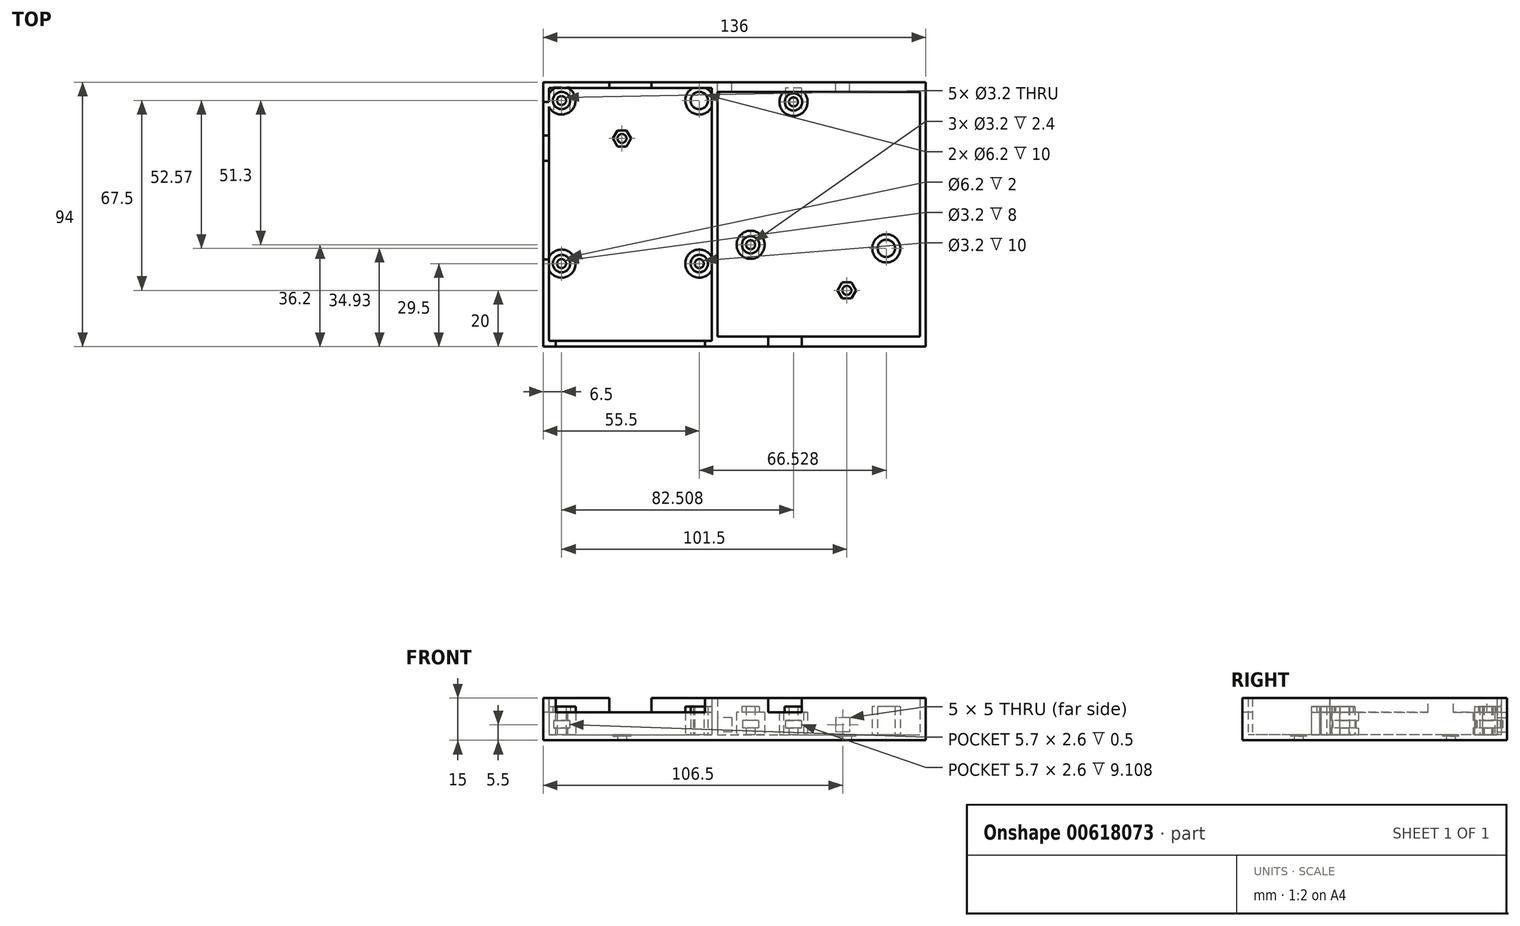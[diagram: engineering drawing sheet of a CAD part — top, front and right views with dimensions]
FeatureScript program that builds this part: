
annotation { "Feature Type Name" : "Feature", "Feature Type Description" : "" }
export const myFeature = defineFeature(function(context is Context, id is Id, definition is map)
    precondition{}
    {
        {
            var Q0;
            Q0=qCreatedBy(makeId("Top.planeOp"),FACE);
            var sketch = newSketch(context, id + "F0", { "sketchPlane" : qUnion([Q0])});
            skLineSegment(sketch, "E0.bottom", {"start": v(-9, 44) * mm, "end": v(-65, 44) * mm, "construction": true});
            skLineSegment(sketch, "E0.top", {"start": v(-9, -44) * mm, "end": v(-65, -44) * mm, "construction": true});
            skLineSegment(sketch, "E0.left", {"start": v(-9, 44) * mm, "end": v(-9, -44) * mm, "construction": true});
            skLineSegment(sketch, "E0.right", {"start": v(-65, 44) * mm, "end": v(-65, -44) * mm, "construction": true});
            skLineSegment(sketch, "E1.bottom", {"start": v(-68, 47) * mm, "end": v(68, 47) * mm});
            skLineSegment(sketch, "E1.top", {"start": v(-68, -47) * mm, "end": v(68, -47) * mm});
            skLineSegment(sketch, "E1.left", {"start": v(-68, 47) * mm, "end": v(-68, -47) * mm});
            skLineSegment(sketch, "E1.right", {"start": v(68, 47) * mm, "end": v(68, -47) * mm});
            skPoint(sketch, "E2", {"position": v(5.77, -10.8) * mm});
            skPoint(sketch, "E3", {"position": v(54.03, -12.07) * mm});
            skPoint(sketch, "E4", {"position": v(21, 40) * mm});
            skPoint(sketch, "E5", {"position": v(-61.5, 40.5) * mm});
            skPoint(sketch, "E6", {"position": v(-12.5, 40.5) * mm});
            skPoint(sketch, "E7", {"position": v(-12.5, -17.5) * mm});
            skPoint(sketch, "E8", {"position": v(-61.5, -17.5) * mm});
            skLineSegment(sketch, "E9.bottom", {"start": v(-61.5, 40.5) * mm, "end": v(-12.5, 40.5) * mm, "construction": true});
            skLineSegment(sketch, "E9.top", {"start": v(-61.5, -17.5) * mm, "end": v(-12.5, -17.5) * mm, "construction": true});
            skLineSegment(sketch, "E9.left", {"start": v(-61.5, 40.5) * mm, "end": v(-61.5, -17.5) * mm, "construction": true});
            skLineSegment(sketch, "E9.right", {"start": v(-12.5, 40.5) * mm, "end": v(-12.5, -17.5) * mm, "construction": true});
            skLineSegment(sketch, "E10.bottom", {"start": v(-8, -45) * mm, "end": v(-66, -45) * mm});
            skLineSegment(sketch, "E10.top", {"start": v(-8, 45) * mm, "end": v(-66, 45) * mm});
            skLineSegment(sketch, "E10.left", {"start": v(-8, -45) * mm, "end": v(-8, 45) * mm});
            skLineSegment(sketch, "E10.right", {"start": v(-66, -45) * mm, "end": v(-66, 45) * mm});
            skLineSegment(sketch, "E11.bottom", {"start": v(66, -43.5) * mm, "end": v(-6, -43.5) * mm});
            skLineSegment(sketch, "E11.top", {"start": v(66, 43.5) * mm, "end": v(-6, 43.5) * mm});
            skLineSegment(sketch, "E11.left", {"start": v(66, -43.5) * mm, "end": v(66, 43.5) * mm});
            skLineSegment(sketch, "E11.right", {"start": v(-6, -43.5) * mm, "end": v(-6, 43.5) * mm});
            skPoint(sketch, "E11.middle", {"position": v(30, 0) * mm});
            skLineSegment(sketch, "E12.bottom", {"start": v(65, -42.5) * mm, "end": v(-5, -42.5) * mm, "construction": true});
            skLineSegment(sketch, "E12.top", {"start": v(65, 42.5) * mm, "end": v(-5, 42.5) * mm, "construction": true});
            skLineSegment(sketch, "E12.left", {"start": v(65, -42.5) * mm, "end": v(65, 42.5) * mm, "construction": true});
            skLineSegment(sketch, "E12.right", {"start": v(-5, -42.5) * mm, "end": v(-5, 42.5) * mm, "construction": true});
            skPoint(sketch, "E13", {"position": v(-37, 0) * mm});
            skPoint(sketch, "E13.positionSnap0", {"position": v(-37, 45) * mm});
            skPoint(sketch, "E13.positionSnap1", {"position": v(-8, 0) * mm});
            skSolve(sketch);
        }
        {
            var Q0;
            Q0=makeQuery(id+"F0.imprint","IMPRINT",FACE,{"disambiguationData":[TD([[makeQuery(id+"F0.imprint","IMPRINT",EDGE,{"derivedFrom":sQuery(id+"F0.wireOp",EDGE,"E1.bottom")}),-1.0]])]});
            var Q1;
            Q1=makeQuery(id+"F0.imprint","IMPRINT",FACE,{"disambiguationData":[TD([[makeQuery(id+"F0.imprint","IMPRINT",EDGE,{"derivedFrom":sQuery(id+"F0.wireOp",EDGE,"E11.bottom")}),-1.0]])]});
            var Q2;
            Q2=makeQuery(id+"F0.imprint","IMPRINT",FACE,{"disambiguationData":[TD([[makeQuery(id+"F0.imprint","IMPRINT",EDGE,{"derivedFrom":sQuery(id+"F0.wireOp",EDGE,"E10.bottom")}),-1.0]])]});
            extrude(context, id + "F1", {"entities" : qUnion([Q0, Q1, Q2]), "depth" : 2 * mm, "offsetDistance" : 25 * mm});
        }
        {
            var Q0;
            Q0=makeQuery(id+"F0.imprint","IMPRINT",FACE,{"disambiguationData":[TD([[makeQuery(id+"F0.imprint","IMPRINT",EDGE,{"derivedFrom":sQuery(id+"F0.wireOp",EDGE,"E1.bottom")}),-1.0]])]});
            extrude(context, id + "F2", {"entities" : qUnion([Q0]), "operationType" : NewBodyOperationType.ADD, "depth" : 15 * mm, "offsetDistance" : 25 * mm});
        }
        {
            var Q0;
            Q0=makeQuery(id+"F2.boolean.opBoolean","SPLIT",FACE,{"disambiguationData":[TD([makeQuery(id+"F2.opExtrude","SWEPT_FACE",FACE,{"disambiguationData":[OSD([sQuery(id+"F0.wireOp",EDGE,"E10.bottom")])]})])],"derivedFrom":makeQuery(id+"F1.opExtrude","CAP_FACE",FACE,{"disambiguationData":[OSD([sQuery(id+"F0.wireOp",EDGE,"E1.bottom"),sQuery(id+"F0.wireOp",EDGE,"E1.top"),sQuery(id+"F0.wireOp",EDGE,"E1.left"),sQuery(id+"F0.wireOp",EDGE,"E1.right")])],"isStart":false})});
            var sketch = newSketch(context, id + "F3", { "sketchPlane" : qUnion([Q0])});
            skCircle(sketch, "E14", {"center": v(-61.5, 40.5) * mm, "radius": 5 * mm});
            skCircle(sketch, "E15", {"center": v(-61.5, 40.5) * mm, "radius": 3.1 * mm});
            skCircle(sketch, "E16", {"center": v(-61.5, 40.5) * mm, "radius": 1.6 * mm});
            skLineSegment(sketch, "E17", {"start": v(-37, 64.72) * mm, "end": v(-37, -33.51) * mm, "construction": true});
            skCircle(sketch, "E18.MirrorC", {"center": v(-12.5, 40.5) * mm, "radius": 5 * mm});
            skCircle(sketch, "E19.MirrorC", {"center": v(-12.5, 40.5) * mm, "radius": 3.1 * mm});
            skCircle(sketch, "E20.MirrorC", {"center": v(-12.5, 40.5) * mm, "radius": 1.6 * mm});
            skLineSegment(sketch, "E21", {"start": v(-88.41, 11.5) * mm, "end": v(-11.99, 11.5) * mm, "construction": true});
            skCircle(sketch, "E22.MirrorC", {"center": v(-61.5, -17.5) * mm, "radius": 5 * mm});
            skCircle(sketch, "E23.MirrorC", {"center": v(-61.5, -17.5) * mm, "radius": 3.1 * mm});
            skCircle(sketch, "E24.MirrorC", {"center": v(-61.5, -17.5) * mm, "radius": 1.6 * mm});
            skCircle(sketch, "E25.MirrorC", {"center": v(-12.5, -17.5) * mm, "radius": 5 * mm});
            skCircle(sketch, "E26.MirrorC", {"center": v(-12.5, -17.5) * mm, "radius": 3.1 * mm});
            skCircle(sketch, "E27.MirrorC", {"center": v(-12.5, -17.5) * mm, "radius": 1.6 * mm});
            skCircle(sketch, "E28", {"center": v(5.77, -10.8) * mm, "radius": 1.6 * mm});
            skCircle(sketch, "E29", {"center": v(5.77, -10.8) * mm, "radius": 3.1 * mm});
            skCircle(sketch, "E30", {"center": v(5.77, -10.8) * mm, "radius": 5 * mm});
            skLineSegment(sketch, "E31", {"start": v(35.4, 26.87) * mm, "end": v(35.4, -34.45) * mm, "construction": true});
            skCircle(sketch, "E32.MirrorC", {"center": v(54.03, -12.07) * mm, "radius": 5 * mm});
            skCircle(sketch, "E33.MirrorC", {"center": v(54.03, -12.07) * mm, "radius": 3.1 * mm});
            skCircle(sketch, "E34.MirrorC", {"center": v(54.03, -12.07) * mm, "radius": 1.6 * mm});
            skCircle(sketch, "E35", {"center": v(21, 40) * mm, "radius": 1.6 * mm});
            skCircle(sketch, "E36", {"center": v(21, 40) * mm, "radius": 3.1 * mm});
            skCircle(sketch, "E37", {"center": v(21, 40) * mm, "radius": 5 * mm});
            skSolve(sketch);
        }
        {
            var Q0;
            Q0=makeQuery(id+"F3.imprint","IMPRINT",FACE,{"disambiguationData":[TD([[makeQuery(id+"F3.imprint","IMPRINT",EDGE,{"derivedFrom":sQuery(id+"F3.wireOp",EDGE,"E15")}),1.0]])]});
            var Q1;
            Q1=makeQuery(id+"F3.imprint","IMPRINT",FACE,{"disambiguationData":[TD([[makeQuery(id+"F3.imprint","IMPRINT",EDGE,{"derivedFrom":sQuery(id+"F3.wireOp",EDGE,"E19.MirrorC")}),-1.0]])]});
            var Q2;
            Q2=makeQuery(id+"F3.imprint","IMPRINT",FACE,{"disambiguationData":[TD([[makeQuery(id+"F3.imprint","IMPRINT",EDGE,{"derivedFrom":sQuery(id+"F3.wireOp",EDGE,"E23.MirrorC")}),-1.0]])]});
            var Q3;
            Q3=makeQuery(id+"F3.imprint","IMPRINT",FACE,{"disambiguationData":[TD([[makeQuery(id+"F3.imprint","IMPRINT",EDGE,{"derivedFrom":sQuery(id+"F3.wireOp",EDGE,"E26.MirrorC")}),1.0]])]});
            var Q4;
            Q4=makeQuery(id+"F3.imprint","IMPRINT",FACE,{"disambiguationData":[TD([[makeQuery(id+"F3.imprint","IMPRINT",EDGE,{"derivedFrom":sQuery(id+"F3.wireOp",EDGE,"E28")}),-1.0]])]});
            var Q5;
            Q5=makeQuery(id+"F3.imprint","IMPRINT",FACE,{"disambiguationData":[TD([[makeQuery(id+"F3.imprint","IMPRINT",EDGE,{"derivedFrom":sQuery(id+"F3.wireOp",EDGE,"E33.MirrorC")}),-1.0]])]});
            var Q6;
            Q6=makeQuery(id+"F3.imprint","IMPRINT",FACE,{"disambiguationData":[TD([[makeQuery(id+"F3.imprint","IMPRINT",EDGE,{"derivedFrom":sQuery(id+"F3.wireOp",EDGE,"E35")}),-1.0]])]});
            extrude(context, id + "F4", {"entities" : qUnion([Q0, Q1, Q2, Q3, Q4, Q5, Q6]), "operationType" : NewBodyOperationType.ADD, "depth" : 10 * mm, "offsetDistance" : 25 * mm});
        }
        {
            var Q0;
            Q0=makeQuery(id+"F3.imprint","IMPRINT",FACE,{"disambiguationData":[TD([[makeQuery(id+"F3.imprint","IMPRINT",EDGE,{"derivedFrom":sQuery(id+"F3.wireOp",EDGE,"E14")}),1.0]])]});
            var Q1;
            Q1=makeQuery(id+"F3.imprint","IMPRINT",FACE,{"disambiguationData":[TD([[makeQuery(id+"F3.imprint","IMPRINT",EDGE,{"derivedFrom":sQuery(id+"F3.wireOp",EDGE,"E18.MirrorC")}),-1.0]])]});
            var Q2;
            Q2=makeQuery(id+"F3.imprint","IMPRINT",FACE,{"disambiguationData":[TD([[makeQuery(id+"F3.imprint","IMPRINT",EDGE,{"derivedFrom":sQuery(id+"F3.wireOp",EDGE,"E29")}),-1.0]])]});
            var Q3;
            Q3=makeQuery(id+"F3.imprint","IMPRINT",FACE,{"disambiguationData":[TD([[makeQuery(id+"F3.imprint","IMPRINT",EDGE,{"derivedFrom":sQuery(id+"F3.wireOp",EDGE,"E32.MirrorC")}),-1.0]])]});
            var Q4;
            Q4=makeQuery(id+"F3.imprint","IMPRINT",FACE,{"disambiguationData":[TD([[makeQuery(id+"F3.imprint","IMPRINT",EDGE,{"derivedFrom":sQuery(id+"F3.wireOp",EDGE,"E36")}),-1.0]])]});
            var Q5;
            Q5=makeQuery(id+"F3.imprint","IMPRINT",FACE,{"disambiguationData":[TD([[makeQuery(id+"F3.imprint","IMPRINT",EDGE,{"derivedFrom":sQuery(id+"F3.wireOp",EDGE,"E23.MirrorC")}),1.0]])]});
            var Q6;
            Q6=makeQuery(id+"F3.imprint","IMPRINT",FACE,{"disambiguationData":[TD([[makeQuery(id+"F3.imprint","IMPRINT",EDGE,{"derivedFrom":sQuery(id+"F3.wireOp",EDGE,"E26.MirrorC")}),-1.0]])]});
            extrude(context, id + "F5", {"entities" : qUnion([Q0, Q1, Q2, Q3, Q4, Q5, Q6]), "operationType" : NewBodyOperationType.ADD, "depth" : 8 * mm, "offsetDistance" : 25 * mm});
        }
        {
            var Q0;
            Q0=qCreatedBy(makeId("Front.planeOp"),FACE);
            var Q1;
            Q1=sQuery(id+"F0.wireOp",VERTEX,"E5");
            cPlane(context, id + "F6", {"entities" : qUnion([Q0, Q1]), "cplaneType" : CPlaneType.PLANE_POINT, "offset" : 25 * mm, "width" : 150 * mm, "height" : 150 * mm});
        }
        {
            var Q0;
            Q0=qCreatedBy(id+"F6.planeOp",FACE);
            var sketch = newSketch(context, id + "F7", { "sketchPlane" : qUnion([Q0])});
            skLineSegment(sketch, "E38.bottom", {"start": v(-64.35, 7) * mm, "end": v(-58.65, 7) * mm});
            skLineSegment(sketch, "E38.top", {"start": v(-64.35, 4.4) * mm, "end": v(-58.65, 4.4) * mm});
            skLineSegment(sketch, "E38.left", {"start": v(-64.35, 7) * mm, "end": v(-64.35, 4.4) * mm});
            skLineSegment(sketch, "E38.right", {"start": v(-58.65, 7) * mm, "end": v(-58.65, 4.4) * mm});
            skPoint(sketch, "E38.middle", {"position": v(-61.5, 5.7) * mm});
            skLineSegment(sketch, "E39", {"start": v(-61.5, 2) * mm, "end": v(-61.5, 9.72) * mm, "construction": true});
            skSolve(sketch);
        }
        {
            var Q0;
            Q0 = qSketchRegion(id + "F7", true);
            extrude(context, id + "F8", {"entities" : qUnion([Q0]), "operationType" : NewBodyOperationType.REMOVE, "endBound" : BoundingType.SYMMETRIC, "oppositeDirection" : true, "depth" : 10 * mm, "offsetDistance" : 25 * mm});
        }
        {
            var Q0;
            Q0=qCreatedBy(makeId("Right.planeOp"),FACE);
            var Q1;
            Q1=sQuery(id+"F3.wireOp",VERTEX,"E17.start");
            cPlane(context, id + "F9", {"entities" : qUnion([Q0, Q1]), "cplaneType" : CPlaneType.PLANE_POINT, "offset" : 25 * mm, "width" : 150 * mm, "height" : 150 * mm});
        }
        {
            var Q0;
            Q0=qCreatedBy(makeId("Front.planeOp"),FACE);
            var Q1;
            Q1=sQuery(id+"F3.wireOp",VERTEX,"E21.start");
            cPlane(context, id + "F10", {"entities" : qUnion([Q0, Q1]), "cplaneType" : CPlaneType.PLANE_POINT, "offset" : 25 * mm, "width" : 150 * mm, "height" : 150 * mm});
        }
        {
            var Q0;
            Q0=qCreatedBy(makeId("Front.planeOp"),FACE);
            var Q1;
            Q1=sQuery(id+"F0.wireOp",VERTEX,"E2");
            cPlane(context, id + "F11", {"entities" : qUnion([Q0, Q1]), "cplaneType" : CPlaneType.PLANE_POINT, "offset" : 25 * mm, "width" : 150 * mm, "height" : 150 * mm});
        }
        {
            var Q0;
            Q0=qCreatedBy(id+"F11.planeOp",FACE);
            var sketch = newSketch(context, id + "F12", { "sketchPlane" : qUnion([Q0])});
            skLineSegment(sketch, "E40.bottom", {"start": v(8.62, 4.4) * mm, "end": v(2.92, 4.4) * mm});
            skLineSegment(sketch, "E40.top", {"start": v(8.62, 7) * mm, "end": v(2.92, 7) * mm});
            skLineSegment(sketch, "E40.left", {"start": v(8.62, 4.4) * mm, "end": v(8.62, 7) * mm});
            skLineSegment(sketch, "E40.right", {"start": v(2.92, 4.4) * mm, "end": v(2.92, 7) * mm});
            skPoint(sketch, "E40.middle", {"position": v(5.77, 5.7) * mm});
            skLineSegment(sketch, "E41", {"start": v(5.77, 2) * mm, "end": v(5.77, 9.72) * mm, "construction": true});
            skSolve(sketch);
        }
        {
            var Q0;
            Q0 = qSketchRegion(id + "F12", true);
            extrude(context, id + "F13", {"entities" : qUnion([Q0]), "operationType" : NewBodyOperationType.REMOVE, "endBound" : BoundingType.SYMMETRIC, "oppositeDirection" : true, "depth" : 15 * mm, "offsetDistance" : 25 * mm});
        }
        {
            var Q0;
            Q0=qCreatedBy(makeId("Right.planeOp"),FACE);
            var Q1;
            Q1=sQuery(id+"F0.wireOp",VERTEX,"E11.middle");
            cPlane(context, id + "F14", {"entities" : qUnion([Q0, Q1]), "cplaneType" : CPlaneType.PLANE_POINT, "offset" : 25 * mm, "width" : 150 * mm, "height" : 150 * mm});
        }
        {
            var Q0;
            Q0=qCreatedBy(makeId("Front.planeOp"),FACE);
            var Q1;
            Q1=sQuery(id+"F0.wireOp",VERTEX,"E4");
            cPlane(context, id + "F15", {"entities" : qUnion([Q0, Q1]), "cplaneType" : CPlaneType.PLANE_POINT, "offset" : 25 * mm, "width" : 150 * mm, "height" : 150 * mm});
        }
        {
            var Q0;
            Q0=qCreatedBy(id+"F15.planeOp",FACE);
            var sketch = newSketch(context, id + "F16", { "sketchPlane" : qUnion([Q0])});
            skLineSegment(sketch, "E42.bottom", {"start": v(23.86, 4.4) * mm, "end": v(18.16, 4.4) * mm});
            skLineSegment(sketch, "E42.top", {"start": v(23.86, 7) * mm, "end": v(18.16, 7) * mm});
            skLineSegment(sketch, "E42.left", {"start": v(23.86, 4.4) * mm, "end": v(23.86, 7) * mm});
            skLineSegment(sketch, "E42.right", {"start": v(18.16, 4.4) * mm, "end": v(18.16, 7) * mm});
            skPoint(sketch, "E42.middle", {"position": v(21, 5.7) * mm});
            skLineSegment(sketch, "E43", {"start": v(21, 0) * mm, "end": v(21, 7.72) * mm, "construction": true});
            skSolve(sketch);
        }
        {
            var Q0;
            Q0 = qSketchRegion(id + "F16", true);
            extrude(context, id + "F17", {"entities" : qUnion([Q0]), "operationType" : NewBodyOperationType.REMOVE, "endBound" : BoundingType.SYMMETRIC, "oppositeDirection" : true, "depth" : 10 * mm, "offsetDistance" : 25 * mm});
        }
        {
            var Q0;
            {var subQ0=sQuery(id+"F0.wireOp",EDGE,"E1.top");Q0=makeQuery(id+"F2.boolean.opBoolean","MERGE",FACE,{"derivedFrom":[makeQuery(id+"F1.opExtrude","SWEPT_FACE",FACE,{"disambiguationData":[OSD([subQ0])]}),makeQuery(id+"F2.opExtrude","SWEPT_FACE",FACE,{"disambiguationData":[OSD([subQ0])]})]});}
            var sketch = newSketch(context, id + "F18", { "sketchPlane" : qUnion([Q0])});
            skLineSegment(sketch, "E44.bottom", {"start": v(-63.5, 10) * mm, "end": v(-10.5, 10) * mm});
            skLineSegment(sketch, "E44.top", {"start": v(-63.5, 15) * mm, "end": v(-10.5, 15) * mm});
            skLineSegment(sketch, "E44.left", {"start": v(-63.5, 10) * mm, "end": v(-63.5, 15) * mm});
            skLineSegment(sketch, "E44.right", {"start": v(-10.5, 10) * mm, "end": v(-10.5, 15) * mm});
            skSolve(sketch);
        }
        {
            var Q0;
            Q0=makeQuery(id+"F18.imprint","IMPRINT",FACE,{"disambiguationData":[TD([[makeQuery(id+"F18.imprint","IMPRINT",EDGE,{"derivedFrom":sQuery(id+"F18.wireOp",EDGE,"E44.bottom")}),1.0]])]});
            extrude(context, id + "F19", {"entities" : qUnion([Q0]), "operationType" : NewBodyOperationType.REMOVE, "endBound" : BoundingType.UP_TO_NEXT, "oppositeDirection" : true, "depth" : 25 * mm, "offsetDistance" : 25 * mm});
        }
        {
            var Q0;
            {var subQ0=sQuery(id+"F0.wireOp",EDGE,"E1.bottom");Q0=makeQuery(id+"F2.boolean.opBoolean","MERGE",FACE,{"derivedFrom":[makeQuery(id+"F1.opExtrude","SWEPT_FACE",FACE,{"disambiguationData":[OSD([subQ0])]}),makeQuery(id+"F2.opExtrude","SWEPT_FACE",FACE,{"disambiguationData":[OSD([subQ0])]})]});}
            var sketch = newSketch(context, id + "F20", { "sketchPlane" : qUnion([Q0])});
            skLineSegment(sketch, "E45.bottom", {"start": v(29.5, 10) * mm, "end": v(44.5, 10) * mm});
            skLineSegment(sketch, "E45.top", {"start": v(29.5, 15) * mm, "end": v(44.5, 15) * mm});
            skLineSegment(sketch, "E45.left", {"start": v(29.5, 10) * mm, "end": v(29.5, 15) * mm});
            skLineSegment(sketch, "E45.right", {"start": v(44.5, 10) * mm, "end": v(44.5, 15) * mm});
            skSolve(sketch);
        }
        {
            var Q0;
            Q0=makeQuery(id+"F20.imprint","IMPRINT",FACE,{"disambiguationData":[TD([[makeQuery(id+"F20.imprint","IMPRINT",EDGE,{"derivedFrom":sQuery(id+"F20.wireOp",EDGE,"E45.bottom")}),1.0]])]});
            extrude(context, id + "F21", {"entities" : qUnion([Q0]), "operationType" : NewBodyOperationType.REMOVE, "endBound" : BoundingType.UP_TO_NEXT, "oppositeDirection" : true, "depth" : 25 * mm, "offsetDistance" : 25 * mm});
        }
        {
            var Q0;
            {var subQ0=sQuery(id+"F0.wireOp",EDGE,"E1.left");Q0=makeQuery(id+"F2.boolean.opBoolean","MERGE",FACE,{"derivedFrom":[makeQuery(id+"F1.opExtrude","SWEPT_FACE",FACE,{"disambiguationData":[OSD([subQ0])]}),makeQuery(id+"F2.opExtrude","SWEPT_FACE",FACE,{"disambiguationData":[OSD([subQ0])]})]});}
            var sketch = newSketch(context, id + "F22", { "sketchPlane" : qUnion([Q0])});
            skLineSegment(sketch, "E46.bottom", {"start": v(-28, 15) * mm, "end": v(-40, 15) * mm});
            skLineSegment(sketch, "E46.top", {"start": v(-28, 10) * mm, "end": v(-40, 10) * mm});
            skLineSegment(sketch, "E46.left", {"start": v(-28, 15) * mm, "end": v(-28, 10) * mm});
            skLineSegment(sketch, "E46.right", {"start": v(-40, 15) * mm, "end": v(-40, 10) * mm});
            skPoint(sketch, "E46.middle", {"position": v(-34, 12.5) * mm});
            skLineSegment(sketch, "E47.bottom", {"start": v(-19, 15) * mm, "end": v(16, 15) * mm});
            skLineSegment(sketch, "E47.top", {"start": v(-19, 10) * mm, "end": v(16, 10) * mm});
            skLineSegment(sketch, "E47.left", {"start": v(-19, 15) * mm, "end": v(-19, 10) * mm});
            skLineSegment(sketch, "E47.right", {"start": v(16, 15) * mm, "end": v(16, 10) * mm});
            skSolve(sketch);
        }
        {
            var Q0;
            Q0=makeQuery(id+"F22.imprint","IMPRINT",FACE,{"disambiguationData":[TD([[makeQuery(id+"F22.imprint","IMPRINT",EDGE,{"derivedFrom":sQuery(id+"F22.wireOp",EDGE,"E46.bottom")}),-1.0]])]});
            var Q1;
            Q1=makeQuery(id+"F22.imprint","IMPRINT",FACE,{"disambiguationData":[TD([[makeQuery(id+"F22.imprint","IMPRINT",EDGE,{"derivedFrom":sQuery(id+"F22.wireOp",EDGE,"E47.bottom")}),-1.0]])]});
            var Q2;
            Q2=makeQuery(id+"F2.opExtrude","SWEPT_FACE",FACE,{"disambiguationData":[OSD([sQuery(id+"F0.wireOp",EDGE,"E10.right")])]});
            extrude(context, id + "F23", {"entities" : qUnion([Q0, Q1]), "operationType" : NewBodyOperationType.REMOVE, "endBound" : BoundingType.UP_TO_SURFACE, "oppositeDirection" : true, "depth" : 25 * mm, "endBoundEntityFace" : qUnion([Q2]), "offsetDistance" : 25 * mm});
        }
        {
            var Q0;
            {var subQ0=sQuery(id+"F0.wireOp",EDGE,"E1.bottom");Q0=makeQuery(id+"F2.boolean.opBoolean","MERGE",FACE,{"derivedFrom":[makeQuery(id+"F1.opExtrude","SWEPT_FACE",FACE,{"disambiguationData":[OSD([subQ0])]}),makeQuery(id+"F2.opExtrude","SWEPT_FACE",FACE,{"disambiguationData":[OSD([subQ0])]})]});}
            var sketch = newSketch(context, id + "F24", { "sketchPlane" : qUnion([Q0])});
            skLineSegment(sketch, "E48.bottom", {"start": v(-41, 8) * mm, "end": v(-36, 8) * mm});
            skLineSegment(sketch, "E48.top", {"start": v(-41, 3) * mm, "end": v(-36, 3) * mm});
            skLineSegment(sketch, "E48.left", {"start": v(-36, 8) * mm, "end": v(-36, 3) * mm});
            skLineSegment(sketch, "E48.right", {"start": v(-41, 8) * mm, "end": v(-41, 3) * mm});
            skLineSegment(sketch, "E49.bottom", {"start": v(1, 8) * mm, "end": v(6, 8) * mm});
            skLineSegment(sketch, "E49.top", {"start": v(1, 3) * mm, "end": v(6, 3) * mm});
            skLineSegment(sketch, "E49.left", {"start": v(6, 8) * mm, "end": v(6, 3) * mm});
            skLineSegment(sketch, "E49.right", {"start": v(1, 8) * mm, "end": v(1, 3) * mm});
            skSolve(sketch);
        }
        {
            var Q0;
            Q0=makeQuery(id+"F24.imprint","IMPRINT",FACE,{"disambiguationData":[TD([[makeQuery(id+"F24.imprint","IMPRINT",EDGE,{"derivedFrom":sQuery(id+"F24.wireOp",EDGE,"E48.bottom")}),-1.0]])]});
            var Q1;
            Q1=makeQuery(id+"F24.imprint","IMPRINT",FACE,{"disambiguationData":[TD([[makeQuery(id+"F24.imprint","IMPRINT",EDGE,{"derivedFrom":sQuery(id+"F24.wireOp",EDGE,"E49.bottom")}),-1.0]])]});
            var Q2;
            Q2=makeQuery(id+"F2.opExtrude","SWEPT_FACE",FACE,{"disambiguationData":[OSD([sQuery(id+"F0.wireOp",EDGE,"E11.top")])]});
            extrude(context, id + "F25", {"entities" : qUnion([Q0, Q1]), "operationType" : NewBodyOperationType.REMOVE, "endBound" : BoundingType.UP_TO_SURFACE, "oppositeDirection" : true, "depth" : 25 * mm, "endBoundEntityFace" : qUnion([Q2]), "offsetDistance" : 25 * mm});
        }
        {
            var Q0;
            {var subQ0=sQuery(id+"F0.wireOp",EDGE,"E1.top");Q0=makeQuery(id+"F2.boolean.opBoolean","MERGE",FACE,{"derivedFrom":[makeQuery(id+"F1.opExtrude","SWEPT_FACE",FACE,{"disambiguationData":[OSD([subQ0])]}),makeQuery(id+"F2.opExtrude","SWEPT_FACE",FACE,{"disambiguationData":[OSD([subQ0])]})]});}
            var sketch = newSketch(context, id + "F26", { "sketchPlane" : qUnion([Q0])});
            skLineSegment(sketch, "E50.bottom", {"start": v(12, 10) * mm, "end": v(24, 10) * mm});
            skLineSegment(sketch, "E50.top", {"start": v(12, 15) * mm, "end": v(24, 15) * mm});
            skLineSegment(sketch, "E50.left", {"start": v(12, 10) * mm, "end": v(12, 15) * mm});
            skLineSegment(sketch, "E50.right", {"start": v(24, 10) * mm, "end": v(24, 15) * mm});
            skSolve(sketch);
        }
        {
            var Q0;
            Q0=makeQuery(id+"F26.imprint","IMPRINT",FACE,{"disambiguationData":[TD([[makeQuery(id+"F26.imprint","IMPRINT",EDGE,{"derivedFrom":sQuery(id+"F26.wireOp",EDGE,"E50.bottom")}),1.0]])]});
            extrude(context, id + "F27", {"entities" : qUnion([Q0]), "operationType" : NewBodyOperationType.REMOVE, "endBound" : BoundingType.UP_TO_NEXT, "oppositeDirection" : true, "depth" : 25 * mm, "offsetDistance" : 25 * mm});
        }
        {
            var Q0;
            Q0=makeQuery(id+"F1.opExtrude","CAP_FACE",FACE,{"disambiguationData":[OSD([sQuery(id+"F0.wireOp",EDGE,"E1.bottom"),sQuery(id+"F0.wireOp",EDGE,"E1.top"),sQuery(id+"F0.wireOp",EDGE,"E1.left"),sQuery(id+"F0.wireOp",EDGE,"E1.right")])],"isStart":true});
            var sketch = newSketch(context, id + "F28", { "sketchPlane" : qUnion([Q0])});
            skPoint(sketch, "E51", {"position": v(-40, -27) * mm});
            skPoint(sketch, "E52.1.0", {"position": v(40, 27) * mm});
            skPoint(sketch, "E52.center", {"position": v(0, 0) * mm});
            skSolve(sketch);
        }
        {
            var Q0;
            Q0=sQuery(id+"F28.wireOp",VERTEX,"E51");
            var Q1;
            Q1=sQuery(id+"F28.wireOp",VERTEX,"E52.1.0");
            var Q2;
            Q2=makeQuery(id+"F1.opExtrude","SWEPT_BODY",BODY,{"disambiguationData":[OSD([sQuery(id+"F0.wireOp",EDGE,"E1.bottom"),sQuery(id+"F0.wireOp",EDGE,"E1.top"),sQuery(id+"F0.wireOp",EDGE,"E1.left"),sQuery(id+"F0.wireOp",EDGE,"E1.right")])]});
            hole(context, id + "F29", {"style" : HoleStyle.SIMPLE, "endStyle" : HoleEndStyle.THROUGH, "holeDiameter" : 3.2 * mm, "majorDiameter" : 5 * mm, "isTappedThrough" : true, "tappedDepth" : 2.3 * mm, "tapClearance" : 3, "startFromSketch" : true, "locations" : qUnion([Q0, Q1]), "scope" : qUnion([Q2])});
        }
        {
            var Q0;
            {var subQ3=makeQuery(id+"F2.opExtrude","SWEPT_FACE",FACE,{"disambiguationData":[OSD([sQuery(id+"F0.wireOp",EDGE,"E10.bottom")])]});var subQ5=makeQuery(id+"F1.opExtrude","CAP_FACE",FACE,{"disambiguationData":[OSD([sQuery(id+"F0.wireOp",EDGE,"E1.bottom"),sQuery(id+"F0.wireOp",EDGE,"E1.top"),sQuery(id+"F0.wireOp",EDGE,"E1.left"),sQuery(id+"F0.wireOp",EDGE,"E1.right")])],"isStart":false});Q0=makeQuery(id+"F5.boolean.opBoolean","SPLIT",FACE,{"disambiguationData":[TD([subQ3])],"derivedFrom":makeQuery(id+"F4.boolean.opBoolean","SPLIT",FACE,{"disambiguationData":[TD([subQ3])],"derivedFrom":makeQuery(id+"F2.boolean.opBoolean","SPLIT",FACE,{"disambiguationData":[TD([subQ3])],"derivedFrom":subQ5})})});}
            var sketch = newSketch(context, id + "F30", { "sketchPlane" : qUnion([Q0])});
            skCircle(sketch, "E53.cCircle", {"center": v(-40, 27) * mm, "radius": 2.85 * mm, "construction": true});
            skLineSegment(sketch, "E53.0", {"start": v(-38.35, 24.15) * mm, "end": v(-41.65, 24.15) * mm});
            skLineSegment(sketch, "E53.1", {"start": v(-41.65, 24.15) * mm, "end": v(-43.3, 27) * mm});
            skLineSegment(sketch, "E53.2", {"start": v(-43.3, 27) * mm, "end": v(-41.65, 29.85) * mm});
            skLineSegment(sketch, "E53.3", {"start": v(-41.65, 29.85) * mm, "end": v(-38.35, 29.85) * mm});
            skLineSegment(sketch, "E53.4", {"start": v(-38.35, 29.85) * mm, "end": v(-36.7, 27) * mm});
            skLineSegment(sketch, "E53.5", {"start": v(-36.7, 27) * mm, "end": v(-38.35, 24.15) * mm});
            skPoint(sketch, "E53.0.midPoint", {"position": v(-40, 24.15) * mm});
            skLineSegment(sketch, "E54.1.0", {"start": v(41.65, -29.85) * mm, "end": v(38.35, -29.85) * mm});
            skLineSegment(sketch, "E54.1.1", {"start": v(43.3, -27) * mm, "end": v(41.65, -29.85) * mm});
            skLineSegment(sketch, "E54.1.2", {"start": v(41.65, -24.15) * mm, "end": v(43.3, -27) * mm});
            skLineSegment(sketch, "E54.1.3", {"start": v(38.35, -24.15) * mm, "end": v(41.65, -24.15) * mm});
            skLineSegment(sketch, "E54.1.4", {"start": v(36.7, -27) * mm, "end": v(38.35, -24.15) * mm});
            skLineSegment(sketch, "E54.1.5", {"start": v(38.35, -29.85) * mm, "end": v(36.7, -27) * mm});
            skPoint(sketch, "E54.center", {"position": v(0, 0) * mm});
            skSolve(sketch);
        }
        {
            var Q0;
            Q0 = qSketchRegion(id + "F30", true);
            extrude(context, id + "F31", {"entities" : qUnion([Q0]), "operationType" : NewBodyOperationType.REMOVE, "oppositeDirection" : true, "depth" : 0.5 * mm, "offsetDistance" : 25 * mm});
        }
    });
